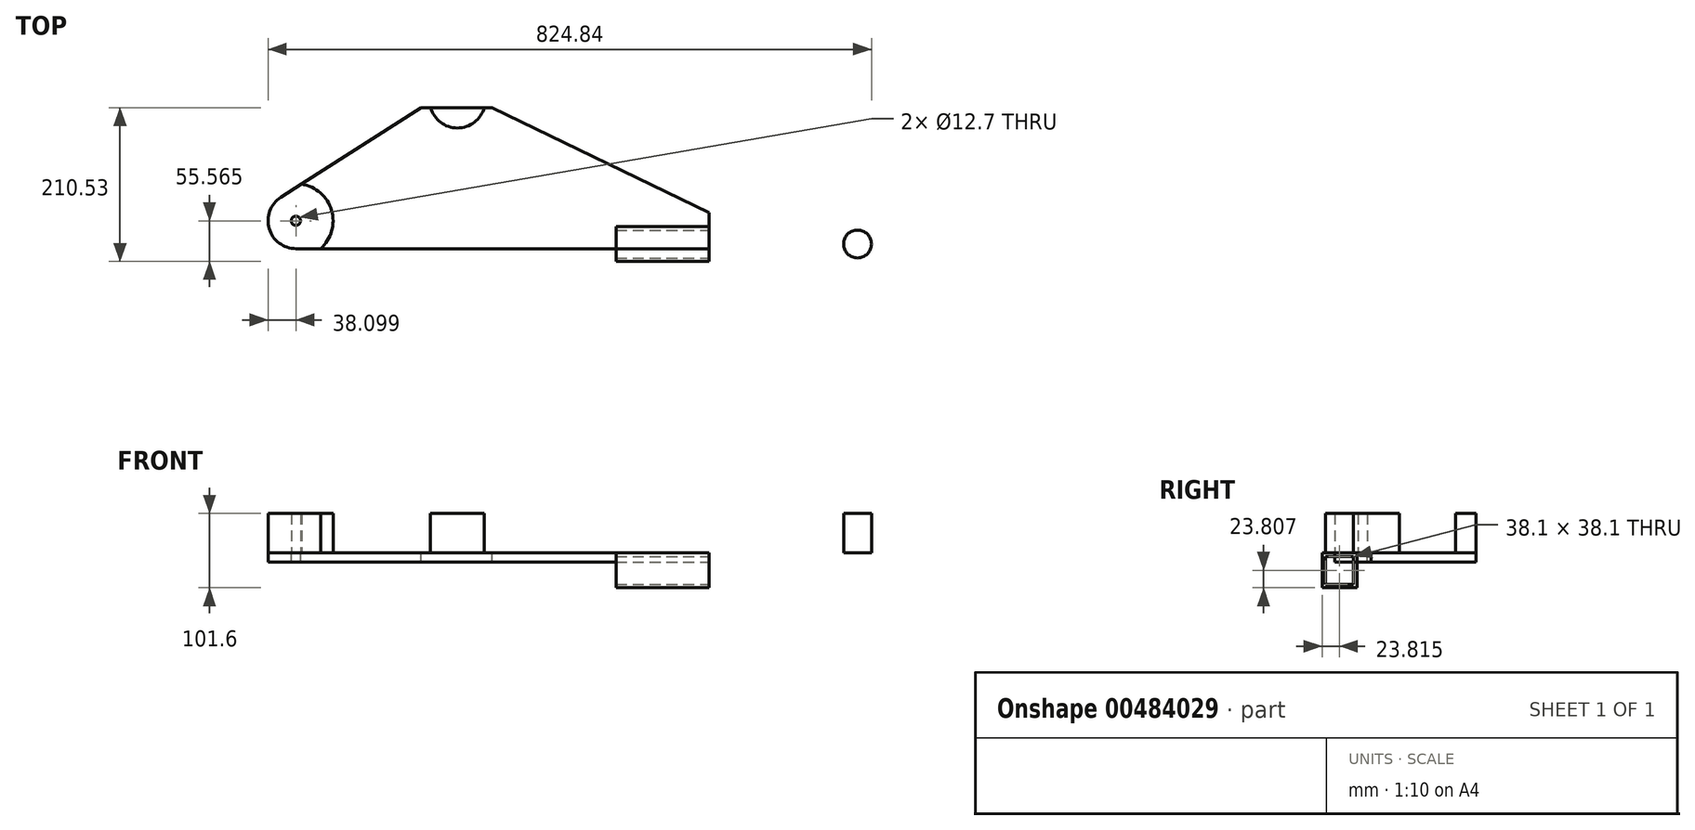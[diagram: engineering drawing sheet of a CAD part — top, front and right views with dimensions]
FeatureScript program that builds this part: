
annotation { "Feature Type Name" : "Feature", "Feature Type Description" : "" }
export const myFeature = defineFeature(function(context is Context, id is Id, definition is map)
    precondition{}
    {
        {
            var Q0;
            Q0=qCreatedBy(makeId("Top.planeOp"),FACE);
            var sketch = newSketch(context, id + "F0", { "sketchPlane" : qUnion([Q0])});
            skArc(sketch, "E0", {"start": v(-291.44, -9.97) * mm, "mid": v(-311.48, -66.93) * mm, "end": v(-262.92, -102.81) * mm});
            skArc(sketch, "E1", {"start": v(504.77, -102.81) * mm, "mid": v(523.48, -87.35) * mm, "end": v(511.8, -66.06) * mm});
            skArc(sketch, "E2", {"start": v(-28.07, 148.5) * mm, "mid": v(-46.28, 150.96) * mm, "end": v(-63.53, 144.62) * mm});
            skLineSegment(sketch, "E3", {"start": v(-262.92, -102.81) * mm, "end": v(504.77, -102.81) * mm});
            skLineSegment(sketch, "E4", {"start": v(511.8, -66.06) * mm, "end": v(-28.07, 148.5) * mm});
            skLineSegment(sketch, "E5", {"start": v(-63.53, 144.62) * mm, "end": v(-291.44, -9.97) * mm});
            skLineSegment(sketch, "E6.bottom", {"start": v(-164.78, -64.34) * mm, "end": v(241.62, -64.34) * mm});
            skLineSegment(sketch, "E6.top", {"start": v(-164.78, -115.14) * mm, "end": v(241.62, -115.14) * mm});
            skLineSegment(sketch, "E6.left", {"start": v(-164.78, -64.34) * mm, "end": v(-164.78, -115.14) * mm});
            skLineSegment(sketch, "E6.right", {"start": v(241.62, -64.34) * mm, "end": v(241.62, -115.14) * mm});
            skCircle(sketch, "E7", {"center": v(-262.92, -52.01) * mm, "radius": 50.8 * mm});
            skCircle(sketch, "E8", {"center": v(-42.14, 113.09) * mm, "radius": 38.1 * mm});
            skCircle(sketch, "E9", {"center": v(504.77, -83.76) * mm, "radius": 19.05 * mm});
            skCircle(sketch, "E10", {"center": v(-262.92, -52.01) * mm, "radius": 38.1 * mm});
            skLineSegment(sketch, "E11.trimOffspring", {"start": v(-262.92, -90.11) * mm, "end": v(301.57, -90.11) * mm});
            skLineSegment(sketch, "E12", {"start": v(-283.5, -19.94) * mm, "end": v(-91.9, 102.95) * mm});
            skLineSegment(sketch, "E13", {"start": v(-91.9, 102.95) * mm, "end": v(5.47, 102.95) * mm});
            skLineSegment(sketch, "E14", {"start": v(5.47, 102.95) * mm, "end": v(301.57, -40.93) * mm});
            skLineSegment(sketch, "E15", {"start": v(301.57, -40.93) * mm, "end": v(301.57, -90.11) * mm});
            skLineSegment(sketch, "E16.bottom", {"start": v(174.57, -59.95) * mm, "end": v(301.57, -59.95) * mm});
            skLineSegment(sketch, "E16.top", {"start": v(174.57, -107.58) * mm, "end": v(301.57, -107.58) * mm});
            skLineSegment(sketch, "E16.left", {"start": v(174.57, -59.95) * mm, "end": v(174.57, -107.58) * mm});
            skLineSegment(sketch, "E16.right", {"start": v(301.57, -59.95) * mm, "end": v(301.57, -107.58) * mm});
            skPoint(sketch, "E17", {"position": v(301.57, -90.11) * mm});
            skCircle(sketch, "E18", {"center": v(-262.92, -52.01) * mm, "radius": 6.35 * mm});
            skSolve(sketch);
        }
        {
            var Q0;
            {var subQ0=sQuery(id+"F0.wireOp",EDGE,"wZ8mWaas-fQSj-fyRA-nvrN-VIoM6lY1kZtV.bottom");Q0=makeQuery(id+"F0.imprint","IMPRINT",FACE,{"disambiguationData":[TD([[makeQuery(id+"F0.imprint","IMPRINT",EDGE,{"derivedFrom":subQ0}),-1.0]])]});}
            var Q1;
            {var subQ0=sQuery(id+"F0.wireOp",EDGE,"wZ8mWaas-fQSj-fyRA-nvrN-VIoM6lY1kZtV.top");var subQ1=sQuery(id+"F0.wireOp",EDGE,"E6.right");var subQ2=makeQuery(id+"F0.imprint","INTERSECT",VERTEX,{"derivedFrom":[subQ1,subQ0]});Q1=makeQuery(id+"F0.imprint","IMPRINT",FACE,{"disambiguationData":[TD([[makeQuery(id+"F0.imprint","IMPRINT",EDGE,{"disambiguationData":[TD([[subQ2,1.0]])],"derivedFrom":subQ1}),1.0]])]});}
            var Q2;
            {var subQ0=sQuery(id+"F0.wireOp",EDGE,"wZ8mWaas-fQSj-fyRA-nvrN-VIoM6lY1kZtV.top");var subQ1=sQuery(id+"F0.wireOp",EDGE,"E6.right");var subQ2=makeQuery(id+"F0.imprint","INTERSECT",VERTEX,{"derivedFrom":[subQ1,subQ0]});Q2=makeQuery(id+"F0.imprint","IMPRINT",FACE,{"disambiguationData":[TD([[makeQuery(id+"F0.imprint","IMPRINT",EDGE,{"disambiguationData":[TD([[subQ2,1.0]])],"derivedFrom":subQ1}),-1.0]])]});}
            var Q3;
            {var subQ0=sQuery(id+"F0.wireOp",EDGE,"E6.right");var subQ1=sQuery(id+"F0.wireOp",EDGE,"E6.bottom");var subQ2=makeQuery(id+"F0.imprint","INTERSECT",VERTEX,{"derivedFrom":[subQ1,subQ0]});Q3=makeQuery(id+"F0.imprint","IMPRINT",FACE,{"disambiguationData":[TD([[makeQuery(id+"F0.imprint","IMPRINT",EDGE,{"disambiguationData":[TD([[subQ2,1.0]])],"derivedFrom":subQ1}),-1.0]])]});}
            var Q4;
            {var subQ8=sQuery(id+"F0.wireOp",EDGE,"E16.bottom");Q4=makeQuery(id+"F0.imprint","IMPRINT",FACE,{"disambiguationData":[TD([[makeQuery(id+"F0.imprint","IMPRINT",EDGE,{"derivedFrom":subQ8}),-1.0]])]});}
            extrude(context, id + "F1", {"entities" : qUnion([Q0, Q1, Q2, Q3, Q4]), "oppositeDirection" : true, "depth" : 47.62 * mm});
        }
        {
            var Q0;
            Q0=makeQuery(id+"F1.opExtrude","SWEPT_FACE",FACE,{"disambiguationData":[OSD([sQuery(id+"F0.wireOp",EDGE,"E16.right")])]});
            var sketch = newSketch(context, id + "F2", { "sketchPlane" : qUnion([Q0])});
            skLineSegment(sketch, "E19.bottom", {"start": v(-102.81, -4.76) * mm, "end": v(-64.71, -4.76) * mm});
            skLineSegment(sketch, "E19.top", {"start": v(-102.81, -42.86) * mm, "end": v(-64.71, -42.86) * mm});
            skLineSegment(sketch, "E19.left", {"start": v(-102.81, -4.76) * mm, "end": v(-102.81, -42.86) * mm});
            skLineSegment(sketch, "E19.right", {"start": v(-64.71, -4.76) * mm, "end": v(-64.71, -42.86) * mm});
            skSolve(sketch);
        }
        {
            var Q0;
            Q0 = qSketchRegion(id + "F2", true);
            extrude(context, id + "F3", {"entities" : qUnion([Q0]), "operationType" : NewBodyOperationType.REMOVE, "endBound" : BoundingType.UP_TO_NEXT, "oppositeDirection" : true, "depth" : 25.4 * mm});
        }
        {
            var Q0;
            {var subQ0=sQuery(id+"F0.wireOp",EDGE,"E14");Q0=makeQuery(id+"F0.imprint","IMPRINT",FACE,{"disambiguationData":[TD([[makeQuery(id+"F0.imprint","IMPRINT",EDGE,{"derivedFrom":subQ0}),-1.0]])]});}
            var Q1;
            {var subQ0=sQuery(id+"F0.wireOp",EDGE,"E12");var subQ1=sQuery(id+"F0.wireOp",EDGE,"E7");var subQ2=makeQuery(id+"F0.imprint","INTERSECT",VERTEX,{"derivedFrom":[subQ1,subQ0]});Q1=makeQuery(id+"F0.imprint","IMPRINT",FACE,{"disambiguationData":[TD([[makeQuery(id+"F0.imprint","IMPRINT",EDGE,{"disambiguationData":[TD([[subQ2,1.0]])],"derivedFrom":subQ1}),1.0]])]});}
            var Q2;
            {var subQ0=sQuery(id+"F0.wireOp",EDGE,"E11.trimOffspring");var subQ1=sQuery(id+"F0.wireOp",EDGE,"E10");var subQ2=makeQuery(id+"F0.imprint","INTERSECT",VERTEX,{"disambiguationData":[OD(0.0)],"derivedFrom":[subQ1,subQ0]});Q2=makeQuery(id+"F0.imprint","IMPRINT",FACE,{"disambiguationData":[TD([[makeQuery(id+"F0.imprint","IMPRINT",EDGE,{"disambiguationData":[TD([[subQ2,1.0]])],"derivedFrom":subQ1}),1.0]])]});}
            var Q3;
            {var subQ0=sQuery(id+"F0.wireOp",EDGE,"wZ8mWaas-fQSj-fyRA-nvrN-VIoM6lY1kZtV.bottom");Q3=makeQuery(id+"F0.imprint","IMPRINT",FACE,{"disambiguationData":[TD([[makeQuery(id+"F0.imprint","IMPRINT",EDGE,{"derivedFrom":subQ0}),-1.0]])]});}
            var Q4;
            {var subQ0=sQuery(id+"F0.wireOp",EDGE,"E6.left");var subQ1=sQuery(id+"F0.wireOp",EDGE,"E6.bottom");var subQ2=makeQuery(id+"F0.imprint","INTERSECT",VERTEX,{"derivedFrom":[subQ1,subQ0]});Q4=makeQuery(id+"F0.imprint","IMPRINT",FACE,{"disambiguationData":[TD([[makeQuery(id+"F0.imprint","IMPRINT",EDGE,{"disambiguationData":[TD([[subQ2,-1.0]])],"derivedFrom":subQ1}),-1.0]])]});}
            var Q5;
            {var subQ0=sQuery(id+"F0.wireOp",EDGE,"E13");var subQ1=sQuery(id+"F0.wireOp",EDGE,"E8");var subQ2=makeQuery(id+"F0.imprint","INTERSECT",VERTEX,{"disambiguationData":[OD(0.0)],"derivedFrom":[subQ1,subQ0]});Q5=makeQuery(id+"F0.imprint","IMPRINT",FACE,{"disambiguationData":[TD([[makeQuery(id+"F0.imprint","IMPRINT",EDGE,{"disambiguationData":[TD([[subQ2,-1.0]])],"derivedFrom":subQ1}),1.0]])]});}
            var Q6;
            {var subQ0=sQuery(id+"F0.wireOp",EDGE,"E6.right");var subQ1=sQuery(id+"F0.wireOp",EDGE,"E6.bottom");var subQ2=makeQuery(id+"F0.imprint","INTERSECT",VERTEX,{"derivedFrom":[subQ1,subQ0]});Q6=makeQuery(id+"F0.imprint","IMPRINT",FACE,{"disambiguationData":[TD([[makeQuery(id+"F0.imprint","IMPRINT",EDGE,{"disambiguationData":[TD([[subQ2,1.0]])],"derivedFrom":subQ1}),-1.0]])]});}
            var Q7;
            {var subQ8=sQuery(id+"F0.wireOp",EDGE,"E16.bottom");Q7=makeQuery(id+"F0.imprint","IMPRINT",FACE,{"disambiguationData":[TD([[makeQuery(id+"F0.imprint","IMPRINT",EDGE,{"derivedFrom":subQ8}),-1.0]])]});}
            extrude(context, id + "F4", {"entities" : qUnion([Q0, Q1, Q2, Q3, Q4, Q5, Q6, Q7]), "oppositeDirection" : true, "depth" : 12.7 * mm});
        }
        {
            var Q0;
            {var subQ0=sQuery(id+"F0.wireOp",EDGE,"E8");var subQ1=makeQuery(id+"F0.imprint","INTERSECT",VERTEX,{"derivedFrom":[sQuery(id+"F0.wireOp",EDGE,"E4"),subQ0]});Q0=makeQuery(id+"F0.imprint","IMPRINT",FACE,{"disambiguationData":[TD([[makeQuery(id+"F0.imprint","IMPRINT",EDGE,{"disambiguationData":[TD([[subQ1,-1.0]])],"derivedFrom":subQ0}),1.0]])]});}
            var Q1;
            {var subQ0=sQuery(id+"F0.wireOp",EDGE,"E7");var subQ1=makeQuery(id+"F0.imprint","INTERSECT",VERTEX,{"derivedFrom":[sQuery(id+"F0.wireOp",EDGE,"E3"),subQ0]});Q1=makeQuery(id+"F0.imprint","IMPRINT",FACE,{"disambiguationData":[TD([[makeQuery(id+"F0.imprint","IMPRINT",EDGE,{"disambiguationData":[TD([[subQ1,1.0]])],"derivedFrom":subQ0}),1.0]])]});}
            var Q2;
            {var subQ0=sQuery(id+"F0.wireOp",EDGE,"E9");var subQ1=makeQuery(id+"F0.imprint","INTERSECT",VERTEX,{"derivedFrom":[sQuery(id+"F0.wireOp",EDGE,"E3"),subQ0]});Q2=makeQuery(id+"F0.imprint","IMPRINT",FACE,{"disambiguationData":[TD([[makeQuery(id+"F0.imprint","IMPRINT",EDGE,{"disambiguationData":[TD([[subQ1,1.0]])],"derivedFrom":subQ0}),1.0]])]});}
            var Q3;
            {var subQ0=sQuery(id+"F0.wireOp",EDGE,"E13");var subQ1=sQuery(id+"F0.wireOp",EDGE,"E8");var subQ2=makeQuery(id+"F0.imprint","INTERSECT",VERTEX,{"disambiguationData":[OD(0.0)],"derivedFrom":[subQ1,subQ0]});Q3=makeQuery(id+"F0.imprint","IMPRINT",FACE,{"disambiguationData":[TD([[makeQuery(id+"F0.imprint","IMPRINT",EDGE,{"disambiguationData":[TD([[subQ2,-1.0]])],"derivedFrom":subQ1}),1.0]])]});}
            var Q4;
            {var subQ0=sQuery(id+"F0.wireOp",EDGE,"E11.trimOffspring");var subQ1=sQuery(id+"F0.wireOp",EDGE,"E10");var subQ2=makeQuery(id+"F0.imprint","INTERSECT",VERTEX,{"disambiguationData":[OD(0.0)],"derivedFrom":[subQ1,subQ0]});Q4=makeQuery(id+"F0.imprint","IMPRINT",FACE,{"disambiguationData":[TD([[makeQuery(id+"F0.imprint","IMPRINT",EDGE,{"disambiguationData":[TD([[subQ2,1.0]])],"derivedFrom":subQ1}),1.0]])]});}
            var Q5;
            {var subQ0=sQuery(id+"F0.wireOp",EDGE,"E12");var subQ1=sQuery(id+"F0.wireOp",EDGE,"E7");var subQ2=makeQuery(id+"F0.imprint","INTERSECT",VERTEX,{"derivedFrom":[subQ1,subQ0]});Q5=makeQuery(id+"F0.imprint","IMPRINT",FACE,{"disambiguationData":[TD([[makeQuery(id+"F0.imprint","IMPRINT",EDGE,{"disambiguationData":[TD([[subQ2,1.0]])],"derivedFrom":subQ1}),1.0]])]});}
            var Q6;
            {var subQ0=sQuery(id+"F0.wireOp",EDGE,"E11.trimOffspring");var subQ1=sQuery(id+"F0.wireOp",EDGE,"E10");var subQ2=makeQuery(id+"F0.imprint","INTERSECT",VERTEX,{"disambiguationData":[OD(0.0)],"derivedFrom":[subQ1,subQ0]});Q6=makeQuery(id+"F0.imprint","IMPRINT",FACE,{"disambiguationData":[TD([[makeQuery(id+"F0.imprint","IMPRINT",EDGE,{"disambiguationData":[TD([[subQ2,-1.0]])],"derivedFrom":subQ1}),1.0]])]});}
            extrude(context, id + "F5", {"entities" : qUnion([Q0, Q1, Q2, Q3, Q4, Q5, Q6]), "depth" : 53.97 * mm});
        }
    });
